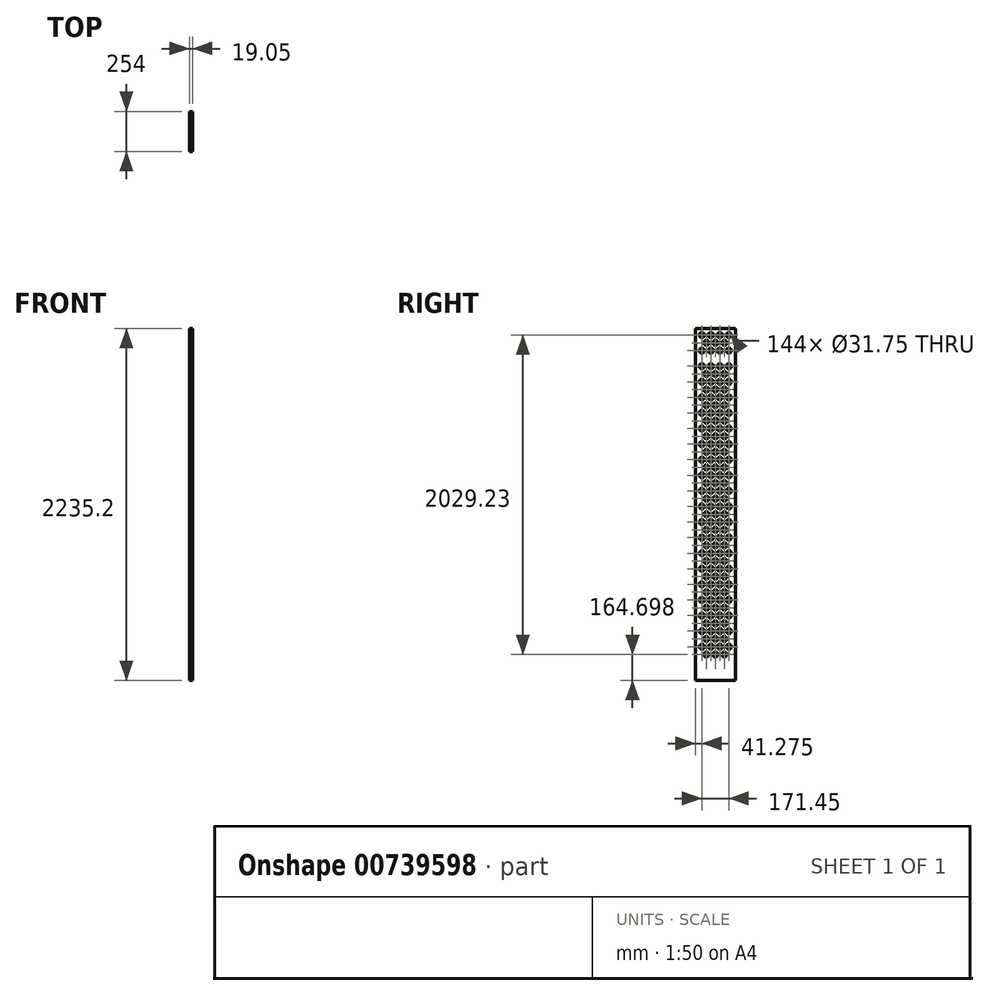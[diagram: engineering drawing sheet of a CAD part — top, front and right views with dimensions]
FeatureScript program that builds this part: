
annotation { "Feature Type Name" : "Feature", "Feature Type Description" : "" }
export const myFeature = defineFeature(function(context is Context, id is Id, definition is map)
    precondition{}
    {
        {
            var Q0;
            Q0=qCreatedBy(makeId("Right.planeOp"),FACE);
            var sketch = newSketch(context, id + "F0", { "sketchPlane" : qUnion([Q0])});
            skLineSegment(sketch, "E0.bottom", {"start": v(127, 1117.6) * mm, "end": v(-127, 1117.6) * mm, "construction": true});
            skLineSegment(sketch, "E0.top", {"start": v(127, -1117.6) * mm, "end": v(-127, -1117.6) * mm, "construction": true});
            skLineSegment(sketch, "E0.left", {"start": v(127, 1117.6) * mm, "end": v(127, -1117.6) * mm, "construction": true});
            skLineSegment(sketch, "E0.right", {"start": v(-127, 1117.6) * mm, "end": v(-127, -1117.6) * mm, "construction": true});
            skPoint(sketch, "E0.middle", {"position": v(0, 0) * mm});
            skLineSegment(sketch, "E1", {"start": v(0, 1117.6) * mm, "end": v(0, 745.07) * mm, "construction": true});
            skLineSegment(sketch, "E2", {"start": v(0, 745.07) * mm, "end": v(0, 372.53) * mm, "construction": true});
            skLineSegment(sketch, "E3", {"start": v(0, 372.53) * mm, "end": v(0, 0) * mm, "construction": true});
            skLineSegment(sketch, "E4.bottom", {"start": v(127, 735.54) * mm, "end": v(-127, 735.54) * mm});
            skLineSegment(sketch, "E4.top", {"start": v(127, 754.6) * mm, "end": v(-127, 754.6) * mm});
            skLineSegment(sketch, "E4.left", {"start": v(127, 735.54) * mm, "end": v(127, 754.6) * mm});
            skLineSegment(sketch, "E4.right", {"start": v(-127, 735.54) * mm, "end": v(-127, 754.6) * mm});
            skPoint(sketch, "E4.middle", {"position": v(0, 745.07) * mm});
            skLineSegment(sketch, "E5.bottom", {"start": v(127, 363) * mm, "end": v(-127, 363) * mm});
            skLineSegment(sketch, "E5.top", {"start": v(127, 382.06) * mm, "end": v(-127, 382.06) * mm});
            skLineSegment(sketch, "E5.left", {"start": v(127, 363) * mm, "end": v(127, 382.06) * mm});
            skLineSegment(sketch, "E5.right", {"start": v(-127, 363) * mm, "end": v(-127, 382.06) * mm});
            skPoint(sketch, "E5.middle", {"position": v(0, 372.53) * mm});
            skLineSegment(sketch, "E6.bottom", {"start": v(-127, 9.52) * mm, "end": v(127, 9.52) * mm});
            skLineSegment(sketch, "E6.top", {"start": v(-127, -9.53) * mm, "end": v(127, -9.53) * mm});
            skLineSegment(sketch, "E6.left", {"start": v(-127, 9.53) * mm, "end": v(-127, -9.53) * mm});
            skLineSegment(sketch, "E6.right", {"start": v(127, 9.52) * mm, "end": v(127, -9.52) * mm});
            skLineSegment(sketch, "E7", {"start": v(-127, 0) * mm, "end": v(127, 0) * mm, "construction": true});
            skLineSegment(sketch, "E8.MirrorCS", {"start": v(127, -382.06) * mm, "end": v(-127, -382.06) * mm});
            skLineSegment(sketch, "E9.MirrorCS", {"start": v(127, -363) * mm, "end": v(-127, -363) * mm});
            skPoint(sketch, "E10.MirrorP", {"position": v(0, -372.53) * mm});
            skLineSegment(sketch, "E11.MirrorCS", {"start": v(127, -363) * mm, "end": v(127, -382.06) * mm});
            skLineSegment(sketch, "E12.MirrorCS", {"start": v(-127, -363) * mm, "end": v(-127, -382.06) * mm});
            skLineSegment(sketch, "E13.MirrorCS", {"start": v(-127, -735.54) * mm, "end": v(-127, -754.6) * mm});
            skLineSegment(sketch, "E14.MirrorCS", {"start": v(127, -735.54) * mm, "end": v(127, -754.6) * mm});
            skPoint(sketch, "E15.MirrorP", {"position": v(0, -745.07) * mm});
            skLineSegment(sketch, "E16.MirrorCS", {"start": v(127, -754.6) * mm, "end": v(-127, -754.6) * mm});
            skLineSegment(sketch, "E17.MirrorCS", {"start": v(127, -735.54) * mm, "end": v(-127, -735.54) * mm});
            skSolve(sketch);
        }
        {
            var Q0;
            Q0=qCreatedBy(makeId("Right.planeOp"),FACE);
            var sketch = newSketch(context, id + "F1", { "sketchPlane" : qUnion([Q0])});
            skLineSegment(sketch, "E18.bottom", {"start": v(127, -1117.6) * mm, "end": v(-127, -1117.6) * mm});
            skLineSegment(sketch, "E18.top", {"start": v(127, 1117.6) * mm, "end": v(-127, 1117.6) * mm});
            skLineSegment(sketch, "E18.left", {"start": v(127, -1117.6) * mm, "end": v(127, 1117.6) * mm});
            skLineSegment(sketch, "E18.right", {"start": v(-127, -1117.6) * mm, "end": v(-127, 1117.6) * mm});
            skPoint(sketch, "E18.middle", {"position": v(0, 0) * mm});
            skLineSegment(sketch, "E19", {"start": v(-114.3, 1076.32) * mm, "end": v(-57.15, 1076.32) * mm, "construction": true});
            skLineSegment(sketch, "E20", {"start": v(-57.15, 1076.32) * mm, "end": v(0, 1076.32) * mm, "construction": true});
            skLineSegment(sketch, "E21", {"start": v(0, 1076.32) * mm, "end": v(57.15, 1076.32) * mm, "construction": true});
            skLineSegment(sketch, "E22", {"start": v(57.15, 1076.32) * mm, "end": v(114.3, 1076.32) * mm, "construction": true});
            skCircle(sketch, "E23", {"center": v(-85.72, 1076.32) * mm, "radius": 15.88 * mm});
            skCircle(sketch, "E24", {"center": v(-28.57, 1076.32) * mm, "radius": 15.88 * mm});
            skCircle(sketch, "E25", {"center": v(28.57, 1076.32) * mm, "radius": 15.88 * mm});
            skPoint(sketch, "E25.perimeterSnap0", {"position": v(28.57, 1076.32) * mm});
            skCircle(sketch, "E26", {"center": v(85.72, 1076.32) * mm, "radius": 15.88 * mm});
            skLineSegment(sketch, "E27", {"start": v(-114.3, 1076.32) * mm, "end": v(-127, 1076.32) * mm, "construction": true});
            skLineSegment(sketch, "E28", {"start": v(114.3, 1076.32) * mm, "end": v(127, 1076.32) * mm, "construction": true});
            skLineSegment(sketch, "E29", {"start": v(-114.3, 1086.11) * mm, "end": v(-101.6, 1086.11) * mm, "construction": true});
            skLineSegment(sketch, "E30", {"start": v(-101.6, 1076.32) * mm, "end": v(-101.6, 1086.11) * mm, "construction": true});
            skLineSegment(sketch, "E31", {"start": v(-114.3, 1076.32) * mm, "end": v(-114.3, 1086.11) * mm, "construction": true});
            skLineSegment(sketch, "E32", {"start": v(-127, 1117.6) * mm, "end": v(-85.72, 1076.32) * mm, "construction": true});
            skCircle(sketch, "E33", {"center": v(-57.15, 1026.83) * mm, "radius": 15.88 * mm});
            skLineSegment(sketch, "E34", {"start": v(-28.57, 1076.32) * mm, "end": v(-57.15, 1026.83) * mm, "construction": true});
            skLineSegment(sketch, "E35", {"start": v(-28.57, 1076.32) * mm, "end": v(-28.57, 1117.6) * mm, "construction": true});
            skPoint(sketch, "E35.endSnap0", {"position": v(0, 1117.6) * mm});
            skLineSegment(sketch, "E36", {"start": v(28.57, 1076.32) * mm, "end": v(28.57, 1117.6) * mm, "construction": true});
            skCircle(sketch, "E37.MirrorC", {"center": v(0, 1026.83) * mm, "radius": 15.88 * mm});
            skCircle(sketch, "E38.MirrorC", {"center": v(57.15, 1026.83) * mm, "radius": 15.88 * mm});
            skLineSegment(sketch, "E39", {"start": v(-57.15, 1026.83) * mm, "end": v(127, 1026.83) * mm, "construction": true});
            skLineSegment(sketch, "E40.MirrorCS", {"start": v(-57.15, 977.34) * mm, "end": v(0, 977.34) * mm, "construction": true});
            skCircle(sketch, "E41.0.1.0", {"center": v(-85.72, 977.34) * mm, "radius": 15.88 * mm});
            skCircle(sketch, "E41.0.1.1", {"center": v(-28.57, 977.34) * mm, "radius": 15.88 * mm});
            skCircle(sketch, "E41.0.1.2", {"center": v(28.57, 977.34) * mm, "radius": 15.88 * mm});
            skCircle(sketch, "E41.0.1.3", {"center": v(85.72, 977.34) * mm, "radius": 15.88 * mm});
            skCircle(sketch, "E41.0.2.0", {"center": v(-85.72, 878.35) * mm, "radius": 15.88 * mm});
            skCircle(sketch, "E41.0.2.1", {"center": v(-28.57, 878.35) * mm, "radius": 15.88 * mm});
            skCircle(sketch, "E41.0.2.2", {"center": v(28.57, 878.35) * mm, "radius": 15.88 * mm});
            skCircle(sketch, "E41.0.2.3", {"center": v(85.72, 878.35) * mm, "radius": 15.88 * mm});
            skCircle(sketch, "E41.0.2.4", {"center": v(57.15, 828.86) * mm, "radius": 15.88 * mm});
            skCircle(sketch, "E41.0.2.5", {"center": v(0, 828.86) * mm, "radius": 15.88 * mm});
            skCircle(sketch, "E41.0.2.6", {"center": v(-57.15, 828.86) * mm, "radius": 15.88 * mm});
            skCircle(sketch, "E41.0.3.0", {"center": v(-85.72, 779.36) * mm, "radius": 15.88 * mm});
            skCircle(sketch, "E41.0.3.1", {"center": v(-28.57, 779.36) * mm, "radius": 15.88 * mm});
            skCircle(sketch, "E41.0.3.2", {"center": v(28.57, 779.36) * mm, "radius": 15.88 * mm});
            skCircle(sketch, "E41.0.3.3", {"center": v(85.72, 779.36) * mm, "radius": 15.88 * mm});
            skCircle(sketch, "E41.0.3.4", {"center": v(57.15, 729.87) * mm, "radius": 15.88 * mm});
            skCircle(sketch, "E41.0.3.5", {"center": v(0, 729.87) * mm, "radius": 15.88 * mm});
            skCircle(sketch, "E41.0.3.6", {"center": v(-57.15, 729.87) * mm, "radius": 15.88 * mm});
            skCircle(sketch, "E41.0.4.0", {"center": v(-85.72, 680.38) * mm, "radius": 15.88 * mm});
            skCircle(sketch, "E41.0.4.1", {"center": v(-28.57, 680.38) * mm, "radius": 15.88 * mm});
            skCircle(sketch, "E41.0.4.2", {"center": v(28.57, 680.38) * mm, "radius": 15.88 * mm});
            skCircle(sketch, "E41.0.4.3", {"center": v(85.72, 680.38) * mm, "radius": 15.88 * mm});
            skCircle(sketch, "E41.0.4.4", {"center": v(57.15, 630.88) * mm, "radius": 15.88 * mm});
            skCircle(sketch, "E41.0.4.5", {"center": v(0, 630.88) * mm, "radius": 15.88 * mm});
            skCircle(sketch, "E41.0.4.6", {"center": v(-57.15, 630.88) * mm, "radius": 15.88 * mm});
            skCircle(sketch, "E41.0.5.0", {"center": v(-85.72, 581.4) * mm, "radius": 15.88 * mm});
            skCircle(sketch, "E41.0.5.1", {"center": v(-28.57, 581.4) * mm, "radius": 15.88 * mm});
            skCircle(sketch, "E41.0.5.2", {"center": v(28.57, 581.4) * mm, "radius": 15.88 * mm});
            skCircle(sketch, "E41.0.5.3", {"center": v(85.72, 581.4) * mm, "radius": 15.88 * mm});
            skCircle(sketch, "E41.0.5.4", {"center": v(57.15, 531.9) * mm, "radius": 15.88 * mm});
            skCircle(sketch, "E41.0.5.5", {"center": v(0, 531.9) * mm, "radius": 15.88 * mm});
            skCircle(sketch, "E41.0.5.6", {"center": v(-57.15, 531.9) * mm, "radius": 15.88 * mm});
            skCircle(sketch, "E41.0.6.0", {"center": v(-85.72, 482.4) * mm, "radius": 15.88 * mm});
            skCircle(sketch, "E41.0.6.1", {"center": v(-28.57, 482.4) * mm, "radius": 15.88 * mm});
            skCircle(sketch, "E41.0.6.2", {"center": v(28.57, 482.4) * mm, "radius": 15.88 * mm});
            skCircle(sketch, "E41.0.6.3", {"center": v(85.72, 482.4) * mm, "radius": 15.88 * mm});
            skCircle(sketch, "E41.0.6.4", {"center": v(57.15, 432.91) * mm, "radius": 15.88 * mm});
            skCircle(sketch, "E41.0.6.5", {"center": v(0, 432.91) * mm, "radius": 15.88 * mm});
            skCircle(sketch, "E41.0.6.6", {"center": v(-57.15, 432.91) * mm, "radius": 15.88 * mm});
            skCircle(sketch, "E41.0.7.0", {"center": v(-85.72, 383.42) * mm, "radius": 15.88 * mm});
            skCircle(sketch, "E41.0.7.1", {"center": v(-28.57, 383.42) * mm, "radius": 15.88 * mm});
            skCircle(sketch, "E41.0.7.2", {"center": v(28.57, 383.42) * mm, "radius": 15.88 * mm});
            skCircle(sketch, "E41.0.7.3", {"center": v(85.72, 383.42) * mm, "radius": 15.88 * mm});
            skCircle(sketch, "E41.0.7.4", {"center": v(57.15, 333.92) * mm, "radius": 15.88 * mm});
            skCircle(sketch, "E41.0.7.5", {"center": v(0, 333.92) * mm, "radius": 15.88 * mm});
            skCircle(sketch, "E41.0.7.6", {"center": v(-57.15, 333.92) * mm, "radius": 15.88 * mm});
            skLineSegment(sketch, "E41.direction1", {"start": v(-85.72, 1076.32) * mm, "end": v(-64.14, 1076.32) * mm, "construction": true});
            skLineSegment(sketch, "E41.direction2", {"start": v(-85.72, 1076.32) * mm, "end": v(-85.72, 977.34) * mm, "construction": true});
            skCircle(sketch, "E42.0.0.8", {"center": v(-85.72, 284.43) * mm, "radius": 15.88 * mm});
            skCircle(sketch, "E42.2.0.8", {"center": v(-28.57, 284.43) * mm, "radius": 15.88 * mm});
            skCircle(sketch, "E42.4.0.8", {"center": v(28.57, 284.43) * mm, "radius": 15.88 * mm});
            skCircle(sketch, "E42.6.0.8", {"center": v(85.72, 284.43) * mm, "radius": 15.88 * mm});
            skCircle(sketch, "E42.8.0.8", {"center": v(57.15, 234.94) * mm, "radius": 15.88 * mm});
            skCircle(sketch, "E42.10.0.8", {"center": v(0, 234.94) * mm, "radius": 15.88 * mm});
            skCircle(sketch, "E42.12.0.8", {"center": v(-57.15, 234.94) * mm, "radius": 15.88 * mm});
            skCircle(sketch, "E42.0.0.9", {"center": v(-85.72, 185.44) * mm, "radius": 15.88 * mm});
            skCircle(sketch, "E42.2.0.9", {"center": v(-28.57, 185.44) * mm, "radius": 15.88 * mm});
            skCircle(sketch, "E42.4.0.9", {"center": v(28.57, 185.44) * mm, "radius": 15.88 * mm});
            skCircle(sketch, "E42.6.0.9", {"center": v(85.72, 185.44) * mm, "radius": 15.88 * mm});
            skCircle(sketch, "E42.8.0.9", {"center": v(57.15, 135.95) * mm, "radius": 15.88 * mm});
            skCircle(sketch, "E42.10.0.9", {"center": v(0, 135.95) * mm, "radius": 15.88 * mm});
            skCircle(sketch, "E42.12.0.9", {"center": v(-57.15, 135.95) * mm, "radius": 15.88 * mm});
            skCircle(sketch, "E42.0.0.10", {"center": v(-85.72, 86.46) * mm, "radius": 15.88 * mm});
            skCircle(sketch, "E42.2.0.10", {"center": v(-28.57, 86.46) * mm, "radius": 15.88 * mm});
            skCircle(sketch, "E42.4.0.10", {"center": v(28.57, 86.46) * mm, "radius": 15.88 * mm});
            skCircle(sketch, "E42.6.0.10", {"center": v(85.72, 86.46) * mm, "radius": 15.88 * mm});
            skCircle(sketch, "E42.8.0.10", {"center": v(57.15, 36.96) * mm, "radius": 15.88 * mm});
            skCircle(sketch, "E42.10.0.10", {"center": v(0, 36.96) * mm, "radius": 15.88 * mm});
            skCircle(sketch, "E42.12.0.10", {"center": v(-57.15, 36.96) * mm, "radius": 15.88 * mm});
            skCircle(sketch, "E42.0.0.11", {"center": v(-85.72, -12.53) * mm, "radius": 15.88 * mm});
            skCircle(sketch, "E42.2.0.11", {"center": v(-28.57, -12.53) * mm, "radius": 15.88 * mm});
            skCircle(sketch, "E42.4.0.11", {"center": v(28.57, -12.53) * mm, "radius": 15.88 * mm});
            skCircle(sketch, "E42.6.0.11", {"center": v(85.72, -12.53) * mm, "radius": 15.88 * mm});
            skCircle(sketch, "E42.8.0.11", {"center": v(57.15, -62.02) * mm, "radius": 15.88 * mm});
            skCircle(sketch, "E42.10.0.11", {"center": v(0, -62.02) * mm, "radius": 15.88 * mm});
            skCircle(sketch, "E42.12.0.11", {"center": v(-57.15, -62.02) * mm, "radius": 15.88 * mm});
            skCircle(sketch, "E42.0.0.12", {"center": v(-85.72, -111.52) * mm, "radius": 15.88 * mm});
            skCircle(sketch, "E42.2.0.12", {"center": v(-28.57, -111.52) * mm, "radius": 15.88 * mm});
            skCircle(sketch, "E42.4.0.12", {"center": v(28.57, -111.52) * mm, "radius": 15.88 * mm});
            skCircle(sketch, "E42.6.0.12", {"center": v(85.72, -111.52) * mm, "radius": 15.88 * mm});
            skCircle(sketch, "E42.8.0.12", {"center": v(57.15, -161) * mm, "radius": 15.88 * mm});
            skCircle(sketch, "E42.10.0.12", {"center": v(0, -161) * mm, "radius": 15.88 * mm});
            skCircle(sketch, "E42.12.0.12", {"center": v(-57.15, -161) * mm, "radius": 15.88 * mm});
            skCircle(sketch, "E42.0.0.13", {"center": v(-85.72, -210.5) * mm, "radius": 15.88 * mm});
            skCircle(sketch, "E42.2.0.13", {"center": v(-28.57, -210.5) * mm, "radius": 15.88 * mm});
            skCircle(sketch, "E42.4.0.13", {"center": v(28.57, -210.5) * mm, "radius": 15.88 * mm});
            skCircle(sketch, "E42.6.0.13", {"center": v(85.72, -210.5) * mm, "radius": 15.88 * mm});
            skCircle(sketch, "E42.8.0.13", {"center": v(57.15, -260) * mm, "radius": 15.88 * mm});
            skCircle(sketch, "E42.10.0.13", {"center": v(0, -260) * mm, "radius": 15.88 * mm});
            skCircle(sketch, "E42.12.0.13", {"center": v(-57.15, -260) * mm, "radius": 15.88 * mm});
            skCircle(sketch, "E42.0.0.14", {"center": v(-85.72, -309.49) * mm, "radius": 15.88 * mm});
            skCircle(sketch, "E42.2.0.14", {"center": v(-28.57, -309.49) * mm, "radius": 15.88 * mm});
            skCircle(sketch, "E42.4.0.14", {"center": v(28.57, -309.49) * mm, "radius": 15.88 * mm});
            skCircle(sketch, "E42.6.0.14", {"center": v(85.72, -309.49) * mm, "radius": 15.88 * mm});
            skCircle(sketch, "E42.8.0.14", {"center": v(57.15, -358.98) * mm, "radius": 15.88 * mm});
            skCircle(sketch, "E42.10.0.14", {"center": v(0, -358.98) * mm, "radius": 15.88 * mm});
            skCircle(sketch, "E42.12.0.14", {"center": v(-57.15, -358.98) * mm, "radius": 15.88 * mm});
            skCircle(sketch, "E42.0.0.15", {"center": v(-85.72, -408.48) * mm, "radius": 15.88 * mm});
            skCircle(sketch, "E42.2.0.15", {"center": v(-28.57, -408.48) * mm, "radius": 15.88 * mm});
            skCircle(sketch, "E42.4.0.15", {"center": v(28.57, -408.48) * mm, "radius": 15.88 * mm});
            skCircle(sketch, "E42.6.0.15", {"center": v(85.72, -408.48) * mm, "radius": 15.88 * mm});
            skCircle(sketch, "E42.8.0.15", {"center": v(57.15, -457.97) * mm, "radius": 15.88 * mm});
            skCircle(sketch, "E42.10.0.15", {"center": v(0, -457.97) * mm, "radius": 15.88 * mm});
            skCircle(sketch, "E42.12.0.15", {"center": v(-57.15, -457.97) * mm, "radius": 15.88 * mm});
            skCircle(sketch, "E42.0.0.16", {"center": v(-85.72, -507.46) * mm, "radius": 15.88 * mm});
            skCircle(sketch, "E42.2.0.16", {"center": v(-28.57, -507.46) * mm, "radius": 15.88 * mm});
            skCircle(sketch, "E42.4.0.16", {"center": v(28.57, -507.46) * mm, "radius": 15.88 * mm});
            skCircle(sketch, "E42.6.0.16", {"center": v(85.72, -507.46) * mm, "radius": 15.88 * mm});
            skCircle(sketch, "E42.8.0.16", {"center": v(57.15, -556.96) * mm, "radius": 15.88 * mm});
            skCircle(sketch, "E42.10.0.16", {"center": v(0, -556.96) * mm, "radius": 15.88 * mm});
            skCircle(sketch, "E42.12.0.16", {"center": v(-57.15, -556.96) * mm, "radius": 15.88 * mm});
            skCircle(sketch, "E42.0.0.17", {"center": v(-85.72, -606.45) * mm, "radius": 15.88 * mm});
            skCircle(sketch, "E42.2.0.17", {"center": v(-28.57, -606.45) * mm, "radius": 15.88 * mm});
            skCircle(sketch, "E42.4.0.17", {"center": v(28.57, -606.45) * mm, "radius": 15.88 * mm});
            skCircle(sketch, "E42.6.0.17", {"center": v(85.72, -606.45) * mm, "radius": 15.88 * mm});
            skCircle(sketch, "E42.8.0.17", {"center": v(57.15, -655.94) * mm, "radius": 15.88 * mm});
            skCircle(sketch, "E42.10.0.17", {"center": v(0, -655.94) * mm, "radius": 15.88 * mm});
            skCircle(sketch, "E42.12.0.17", {"center": v(-57.15, -655.94) * mm, "radius": 15.88 * mm});
            skCircle(sketch, "E42.0.0.18", {"center": v(-85.72, -705.44) * mm, "radius": 15.88 * mm});
            skCircle(sketch, "E42.2.0.18", {"center": v(-28.57, -705.44) * mm, "radius": 15.88 * mm});
            skCircle(sketch, "E42.4.0.18", {"center": v(28.57, -705.44) * mm, "radius": 15.88 * mm});
            skCircle(sketch, "E42.6.0.18", {"center": v(85.72, -705.44) * mm, "radius": 15.88 * mm});
            skCircle(sketch, "E42.8.0.18", {"center": v(57.15, -754.93) * mm, "radius": 15.88 * mm});
            skCircle(sketch, "E42.10.0.18", {"center": v(0, -754.93) * mm, "radius": 15.88 * mm});
            skCircle(sketch, "E42.12.0.18", {"center": v(-57.15, -754.93) * mm, "radius": 15.88 * mm});
            skCircle(sketch, "E42.0.0.19", {"center": v(-85.72, -804.42) * mm, "radius": 15.88 * mm});
            skCircle(sketch, "E42.2.0.19", {"center": v(-28.57, -804.42) * mm, "radius": 15.88 * mm});
            skCircle(sketch, "E42.4.0.19", {"center": v(28.57, -804.42) * mm, "radius": 15.88 * mm});
            skCircle(sketch, "E42.6.0.19", {"center": v(85.72, -804.42) * mm, "radius": 15.88 * mm});
            skCircle(sketch, "E42.8.0.19", {"center": v(57.15, -853.92) * mm, "radius": 15.88 * mm});
            skCircle(sketch, "E42.10.0.19", {"center": v(0, -853.92) * mm, "radius": 15.88 * mm});
            skCircle(sketch, "E42.12.0.19", {"center": v(-57.15, -853.92) * mm, "radius": 15.88 * mm});
            skCircle(sketch, "E43.0.0.20", {"center": v(-85.72, -903.4) * mm, "radius": 15.88 * mm});
            skCircle(sketch, "E43.2.0.20", {"center": v(-28.57, -903.4) * mm, "radius": 15.88 * mm});
            skCircle(sketch, "E43.4.0.20", {"center": v(28.57, -903.4) * mm, "radius": 15.88 * mm});
            skCircle(sketch, "E43.6.0.20", {"center": v(85.72, -903.4) * mm, "radius": 15.88 * mm});
            skCircle(sketch, "E43.8.0.20", {"center": v(57.15, -952.9) * mm, "radius": 15.88 * mm});
            skCircle(sketch, "E43.10.0.20", {"center": v(0, -952.9) * mm, "radius": 15.88 * mm});
            skCircle(sketch, "E43.12.0.20", {"center": v(-57.15, -952.9) * mm, "radius": 15.88 * mm});
            skLineSegment(sketch, "E44", {"start": v(0, 1026.83) * mm, "end": v(0, 828.86) * mm, "construction": true});
            skLineSegment(sketch, "E45.bottom", {"start": v(127, 918.32) * mm, "end": v(-127, 918.32) * mm, "construction": true});
            skLineSegment(sketch, "E45.top", {"start": v(127, 937.37) * mm, "end": v(-127, 937.37) * mm, "construction": true});
            skLineSegment(sketch, "E45.left", {"start": v(127, 918.32) * mm, "end": v(127, 937.37) * mm, "construction": true});
            skLineSegment(sketch, "E45.right", {"start": v(-127, 918.32) * mm, "end": v(-127, 937.37) * mm, "construction": true});
            skPoint(sketch, "E45.middle", {"position": v(0, 927.84) * mm});
            skLineSegment(sketch, "E46", {"start": v(-28.57, 977.34) * mm, "end": v(-28.57, 1026.83) * mm, "construction": true});
            skLineSegment(sketch, "E47.bottom", {"start": v(-127, 992.56) * mm, "end": v(69.85, 992.56) * mm, "construction": true});
            skLineSegment(sketch, "E47.top", {"start": v(-127, 1011.6) * mm, "end": v(69.85, 1011.6) * mm, "construction": true});
            skLineSegment(sketch, "E47.left", {"start": v(-127, 992.56) * mm, "end": v(-127, 1011.6) * mm, "construction": true});
            skLineSegment(sketch, "E47.right", {"start": v(69.85, 992.56) * mm, "end": v(69.85, 1011.6) * mm, "construction": true});
            skPoint(sketch, "E47.middle", {"position": v(-28.57, 1002.08) * mm});
            skCircle(sketch, "E48", {"center": v(0, 927.84) * mm, "radius": 15.88 * mm, "construction": true});
            skSolve(sketch);
        }
        {
            var Q0;
            Q0=qSketchRegion(id+"F1",true);
            extrude(context, id + "F2", {"entities" : qUnion([Q0]), "depth" : 19.05 * mm, "offsetDistance" : 25.4 * mm});
        }
    });
